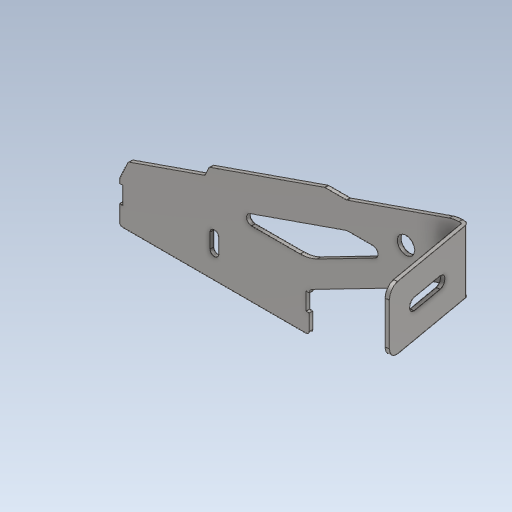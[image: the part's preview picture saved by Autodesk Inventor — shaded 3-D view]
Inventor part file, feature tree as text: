
AUTODESK INVENTOR PART (.ipt)
format: ipt  version: 2020 (Build 240168000, 168)  size: 220,160 bytes
history: native  units: mm
features: other x4, sketch x1, plane x1
ambient origin geometry x8: Origin, YZ Plane, XZ Plane, XY Plane, X Axis, Y Axis, Z Axis, Center Point
bodies: Body1 (feature_tree)
feature tree (6):
  other  "吊架-短(R)#01.05)- 焊接件-1.ipt"
  other  "實體1::吊架-短(R)#01.05)- 焊接件-1.ipt"
  other  "標籤特徵1"
  sketch  "草圖1"
  plane  "工作平面1"
  other  "實體1"
